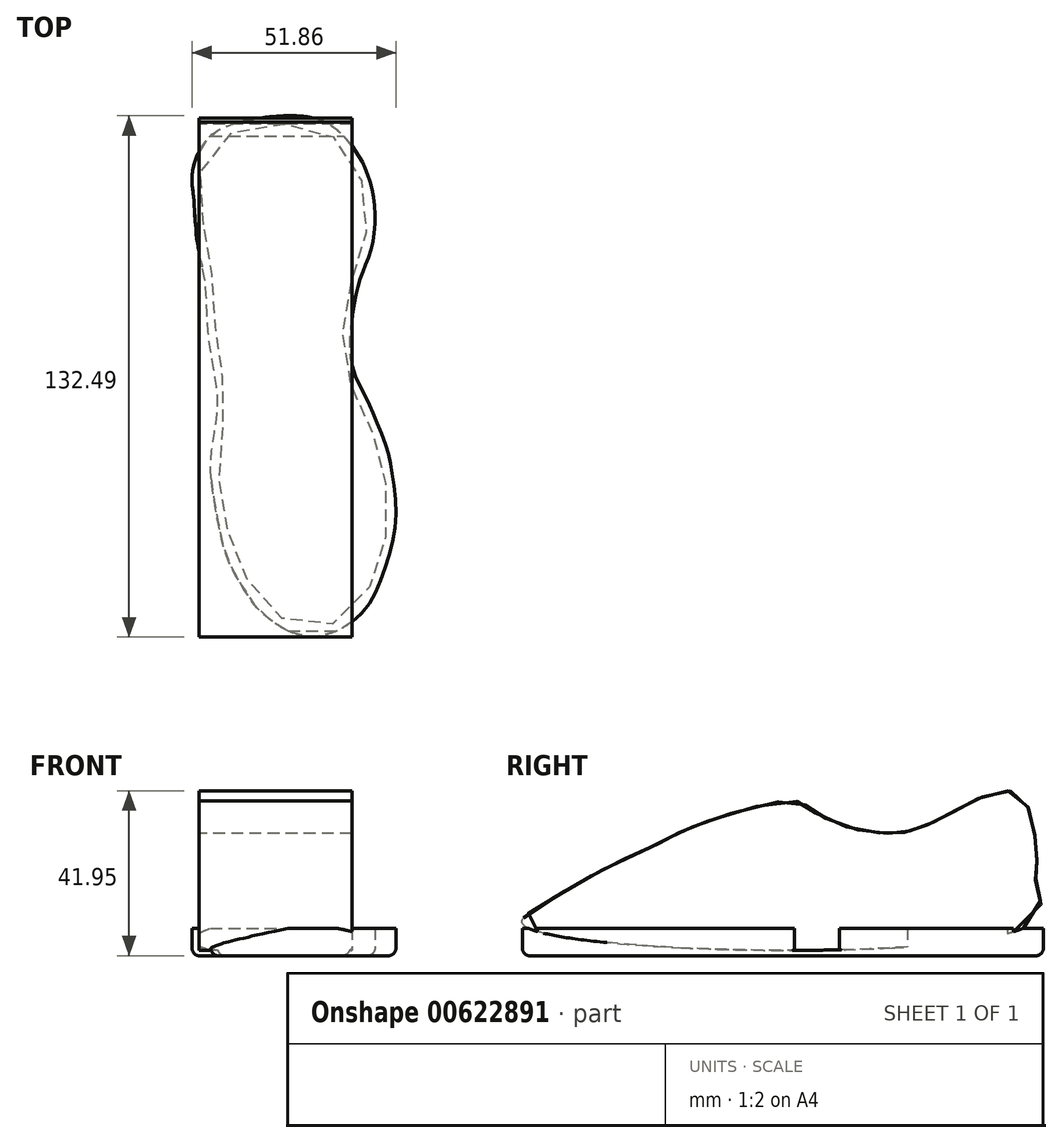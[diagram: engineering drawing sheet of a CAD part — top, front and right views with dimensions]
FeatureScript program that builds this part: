
annotation { "Feature Type Name" : "Feature", "Feature Type Description" : "" }
export const myFeature = defineFeature(function(context is Context, id is Id, definition is map)
    precondition{}
    {
        {
            var Q0;
            Q0=qCreatedBy(makeId("Top.planeOp"),FACE);
            var sketch = newSketch(context, id + "F0", { "sketchPlane" : qUnion([Q0])});
            skFitSpline(sketch, "E0", {"points": [v(-39.72, 43.55) * mm, v(-40.28, 51.6) * mm, v(-40.51, 56.95) * mm, v(-36.79, 65.33) * mm, v(-30.04, 69.29) * mm, v(-22.12, 70.92) * mm, v(-11.88, 71.15) * mm, v(-5.12, 68.82) * mm, v(0, 63.7) * mm, v(3.26, 58.35) * mm, v(5.59, 50.2) * mm, v(5.12, 38.32) * mm, v(2.1, 29.7) * mm, v(0, 19.47) * mm, v(0, 8.06) * mm, v(3.49, 0) * mm, v(5.82, -5.22) * mm, v(8.85, -13.13) * mm, v(10.24, -19.42) * mm, v(11.18, -31.52) * mm, v(8.38, -43.86) * mm, v(3.73, -53.64) * mm, v(-4.66, -59.93) * mm, v(-13.28, -60.63) * mm, v(-22.82, -55.04) * mm, v(-26.78, -49.91) * mm, v(-31.43, -41.53) * mm, v(-34.47, -29.2) * mm, v(-35.81, -16.39) * mm, v(-34.23, -3.58) * mm, v(-34.7, 4.1) * mm, v(-35.86, 11.08) * mm, v(-36.79, 19.23) * mm, v(-37.25, 29.01) * mm, v(-38.65, 35.76) * mm, v(-39.72, 43.55) * mm]});
            skSolve(sketch);
        }
        {
            var Q0;
            Q0=makeQuery(id+"F0.imprint","IMPRINT",FACE,{"disambiguationData":[TD([[makeQuery(id+"F0.imprint","IMPRINT",EDGE,{"derivedFrom":sQuery(id+"F0.wireOp",EDGE,"E0")}),-1.0]])]});
            extrude(context, id + "F1", {"entities" : qUnion([Q0]), "depth" : 7 * mm, "offsetDistance" : 25.4 * mm});
        }
        {
            var Q0;
            Q0=makeQuery(id+"F1.opExtrude","CAP_EDGE",EDGE,{"disambiguationData":[OSD([sQuery(id+"F0.wireOp",EDGE,"E0")])],"isStart":true});
            fillet(context, id + "F2", {"entities" : qUnion([Q0]), "radius" : 2.03 * mm, "tangentPropagation" : true, "allowEdgeOverflow" : false});
        }
        {
            var Q0;
            Q0=qCreatedBy(makeId("Right.planeOp"),FACE);
            var sketch = newSketch(context, id + "F3", { "sketchPlane" : qUnion([Q0])});
            skFitSpline(sketch, "E1", {"points": [v(-55.92, 13.1) * mm, v(-38.03, 23.19) * mm, v(-28.5, 27.53) * mm, v(-22.73, 30.52) * mm, v(-14.78, 33.94) * mm, v(8, 39.36) * mm, v(12.63, 36.82) * mm, v(23.91, 32.06) * mm, v(33.76, 31.17) * mm, v(39, 32.18) * mm, v(47.07, 35.82) * mm, v(54.9, 40) * mm, v(64, 41.56) * mm, v(68.45, 34.54) * mm, v(69.51, 26.1) * mm, v(69.68, 21.1) * mm, v(69.38, 17.3) * mm, v(68.84, 8.43) * mm, v(-60.45, 7.53) * mm, v(-55.92, 13.1) * mm]});
            skLineSegment(sketch, "E2", {"start": v(0, -11.22) * mm, "end": v(0, -67.88) * mm, "construction": true});
            skSolve(sketch);
        }
        {
            var Q0;
            Q0=makeQuery(id+"F3.imprint","IMPRINT",FACE,{"disambiguationData":[TD([[makeQuery(id+"F3.imprint","IMPRINT",EDGE,{"derivedFrom":sQuery(id+"F3.wireOp",EDGE,"E1")}),-1.0]])]});
            extrude(context, id + "F4", {"entities" : qUnion([Q0]), "operationType" : NewBodyOperationType.ADD, "oppositeDirection" : true, "depth" : 38.86 * mm, "offsetDistance" : 25.4 * mm});
        }
    });
